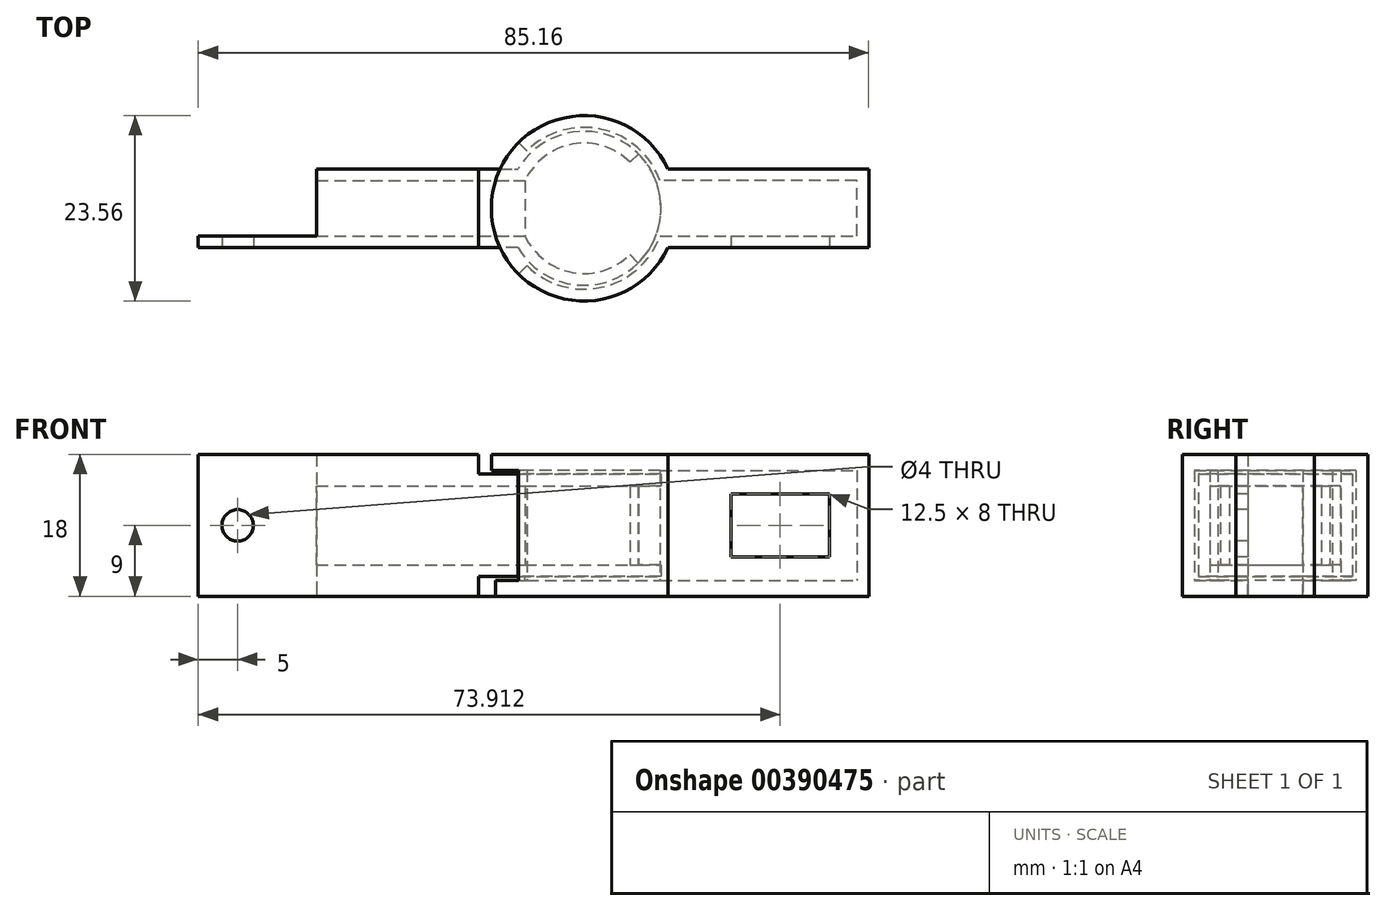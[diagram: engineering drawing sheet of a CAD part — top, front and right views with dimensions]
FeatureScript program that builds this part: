
annotation { "Feature Type Name" : "Feature", "Feature Type Description" : "" }
export const myFeature = defineFeature(function(context is Context, id is Id, definition is map)
    precondition{}
    {
        {
            var Q0;
            Q0=qCreatedBy(makeId("Top.planeOp"),FACE);
            var sketch = newSketch(context, id + "F0", { "sketchPlane" : qUnion([Q0])});
            skLineSegment(sketch, "E0.bottom", {"start": v(-25, 3.5) * mm, "end": v(0, 3.5) * mm});
            skLineSegment(sketch, "E0.top", {"start": v(-25, -3.5) * mm, "end": v(0, -3.5) * mm});
            skLineSegment(sketch, "E0.left", {"start": v(-25, 3.5) * mm, "end": v(-25, -3.5) * mm});
            skLineSegment(sketch, "E0.right", {"start": v(0, 3.5) * mm, "end": v(0, -3.5) * mm});
            skArc(sketch, "E1", {"start": v(0, -3.5) * mm, "mid": v(6.06, -8.15) * mm, "end": v(13.35, -5.85) * mm});
            skPoint(sketch, "E1.centerSnap0", {"position": v(0, 0) * mm});
            skLineSegment(sketch, "E2.left", {"start": v(-25, -3.5) * mm, "end": v(-25, 4) * mm});
            skLineSegment(sketch, "E3", {"start": v(7.5, 0) * mm, "end": v(13.35, 5.85) * mm});
            skLineSegment(sketch, "E4", {"start": v(7.5, 0) * mm, "end": v(13.35, -5.85) * mm});
            skLineSegment(sketch, "E5", {"start": v(7.5, 0) * mm, "end": v(15.78, 0) * mm});
            skArc(sketch, "E6.trimOffspring", {"start": v(13.35, 5.85) * mm, "mid": v(6.06, 8.15) * mm, "end": v(0, 3.5) * mm});
            skArc(sketch, "E7.0", {"start": v(14.41, 6.91) * mm, "mid": v(6.29, 9.7) * mm, "end": v(-0.9, 5) * mm});
            skArc(sketch, "E7.1", {"start": v(-0.9, -5) * mm, "mid": v(6.25, -9.7) * mm, "end": v(14.36, -6.97) * mm});
            skLineSegment(sketch, "E7.2", {"start": v(-26.5, -5) * mm, "end": v(-0.9, -5) * mm});
            skLineSegment(sketch, "E7.3", {"start": v(-26.5, 5) * mm, "end": v(-26.5, -5) * mm});
            skLineSegment(sketch, "E7.4", {"start": v(-26.5, 5) * mm, "end": v(-0.9, 5) * mm});
            skLineSegment(sketch, "E8", {"start": v(13.35, 5.85) * mm, "end": v(14.41, 6.91) * mm});
            skLineSegment(sketch, "E9", {"start": v(13.35, -5.85) * mm, "end": v(14.36, -6.97) * mm});
            skLineSegment(sketch, "E10.bottom", {"start": v(-26.5, -5) * mm, "end": v(-41.5, -5) * mm});
            skLineSegment(sketch, "E10.top", {"start": v(-26.5, -3.5) * mm, "end": v(-41.5, -3.5) * mm});
            skLineSegment(sketch, "E10.left", {"start": v(-26.5, -5) * mm, "end": v(-26.5, -3.5) * mm});
            skLineSegment(sketch, "E10.right", {"start": v(-41.5, -5) * mm, "end": v(-41.5, -3.5) * mm});
            skArc(sketch, "E11", {"start": v(14.41, 6.91) * mm, "mid": v(17.28, -0.04) * mm, "end": v(14.36, -6.97) * mm});
            skLineSegment(sketch, "E12", {"start": v(-5.9, 5) * mm, "end": v(-5.9, -5) * mm});
            skSolve(sketch);
        }
        {
            var Q0;
            Q0=qCreatedBy(makeId("Top.planeOp"),FACE);
            cPlane(context, id + "F1", {"entities" : qUnion([Q0]), "cplaneType" : CPlaneType.OFFSET, "offset" : 0.5 * mm, "oppositeDirection" : true, "width" : 150 * mm, "height" : 150 * mm});
        }
        {
            var Q0;
            Q0=qCreatedBy(id+"F1.planeOp",FACE);
            var sketch = newSketch(context, id + "F2", { "sketchPlane" : qUnion([Q0])});
            skPoint(sketch, "E13.0", {"position": v(7.5, 0) * mm});
            skArc(sketch, "E14.0", {"start": v(14.41, 6.91) * mm, "mid": v(6.29, 9.7) * mm, "end": v(-0.9, 5) * mm});
            skArc(sketch, "E15", {"start": v(17.16, 3.5) * mm, "mid": v(9.73, 10.03) * mm, "end": v(0.23, 7.27) * mm});
            skLineSegment(sketch, "E16", {"start": v(7.5, 0) * mm, "end": v(0.23, 7.27) * mm});
            skLineSegment(sketch, "E17", {"start": v(7.5, 0) * mm, "end": v(0.23, -7.27) * mm});
            skLineSegment(sketch, "E18", {"start": v(7.5, 0) * mm, "end": v(-2.78, 0) * mm});
            skLineSegment(sketch, "E19", {"start": v(17.16, -3.5) * mm, "end": v(42.16, -3.5) * mm});
            skLineSegment(sketch, "E20", {"start": v(42.16, -3.5) * mm, "end": v(42.16, 3.5) * mm});
            skLineSegment(sketch, "E21", {"start": v(42.16, 3.5) * mm, "end": v(17.16, 3.5) * mm});
            skArc(sketch, "E22.trimOffspring", {"start": v(0.23, -7.27) * mm, "mid": v(9.73, -10.03) * mm, "end": v(17.16, -3.5) * mm});
            skArc(sketch, "E23.0", {"start": v(18.16, 5) * mm, "mid": v(9.53, 11.6) * mm, "end": v(-0.83, 8.33) * mm});
            skArc(sketch, "E23.1", {"start": v(-0.83, -8.33) * mm, "mid": v(9.53, -11.6) * mm, "end": v(18.16, -5) * mm});
            skLineSegment(sketch, "E23.2", {"start": v(18.16, -5) * mm, "end": v(43.66, -5) * mm});
            skLineSegment(sketch, "E23.3", {"start": v(43.66, -5) * mm, "end": v(43.66, 5) * mm});
            skLineSegment(sketch, "E23.4", {"start": v(43.66, 5) * mm, "end": v(18.16, 5) * mm});
            skLineSegment(sketch, "E24", {"start": v(0.23, 7.27) * mm, "end": v(-0.83, 8.33) * mm});
            skLineSegment(sketch, "E25", {"start": v(-0.83, -8.33) * mm, "end": v(0.23, -7.27) * mm});
            skPoint(sketch, "E26", {"position": v(42.16, 0) * mm});
            skArc(sketch, "E27", {"start": v(-0.83, 8.33) * mm, "mid": v(-4.28, 0) * mm, "end": v(-0.83, -8.33) * mm});
            skSolve(sketch);
        }
        {
            var Q0;
            Q0=makeQuery(id+"F0.imprint","IMPRINT",FACE,{"disambiguationData":[TD([[makeQuery(id+"F0.imprint","IMPRINT",EDGE,{"derivedFrom":sQuery(id+"F0.wireOp",EDGE,"E0.bottom")}),1.0]])]});
            var Q1;
            Q1=makeQuery(id+"F0.imprint","IMPRINT",FACE,{"disambiguationData":[TD([[makeQuery(id+"F0.imprint","IMPRINT",EDGE,{"derivedFrom":sQuery(id+"F0.wireOp",EDGE,"E10.bottom")}),-1.0]])]});
            var Q2;
            {var subQ0=sQuery(id+"F0.wireOp",EDGE,"E0.left");Q2=makeQuery(id+"F0.imprint","IMPRINT",FACE,{"disambiguationData":[TD([[makeQuery(id+"F0.imprint","IMPRINT",EDGE,{"derivedFrom":subQ0}),-1.0]])]});}
            var Q3;
            {var subQ4=sQuery(id+"F0.wireOp",EDGE,"E1");Q3=makeQuery(id+"F0.imprint","IMPRINT",FACE,{"disambiguationData":[TD([[makeQuery(id+"F0.imprint","IMPRINT",EDGE,{"derivedFrom":subQ4}),-1.0]])]});}
            var Q4;
            {var subQ13=sQuery(id+"F0.wireOp",EDGE,"E7.3");Q4=makeQuery(id+"F0.imprint","IMPRINT",FACE,{"disambiguationData":[TD([[makeQuery(id+"F0.imprint","IMPRINT",EDGE,{"derivedFrom":subQ13}),1.0]])]});}
            extrude(context, id + "F3", {"entities" : qUnion([Q0, Q1, Q2, Q3, Q4]), "depth" : 11.5 * mm});
        }
        {
            var Q0;
            Q0=makeQuery(id+"F3.opExtrude","CAP_FACE",FACE,{"disambiguationData":[OSD([sQuery(id+"F0.wireOp",EDGE,"E10.bottom"),sQuery(id+"F0.wireOp",EDGE,"E10.top"),sQuery(id+"F0.wireOp",EDGE,"E10.left"),sQuery(id+"F0.wireOp",EDGE,"E10.right")])],"isStart":false});
            var Q1;
            {var subQ0=sQuery(id+"F0.wireOp",EDGE,"E0.left");Q1=makeQuery(id+"F0.imprint","IMPRINT",FACE,{"disambiguationData":[TD([[makeQuery(id+"F0.imprint","IMPRINT",EDGE,{"derivedFrom":subQ0}),-1.0]])]});}
            var Q2;
            Q2=makeQuery(id+"F3.opExtrude","CAP_FACE",FACE,{"disambiguationData":[OSD([sQuery(id+"F0.wireOp",EDGE,"E0.bottom"),sQuery(id+"F0.wireOp",EDGE,"E6.trimOffspring"),sQuery(id+"F0.wireOp",EDGE,"E7.0"),sQuery(id+"F0.wireOp",EDGE,"E7.4"),sQuery(id+"F0.wireOp",EDGE,"E8"),sQuery(id+"F0.wireOp",EDGE,"E12")])],"isStart":false});
            var Q3;
            {var subQ4=sQuery(id+"F0.wireOp",EDGE,"E1");Q3=makeQuery(id+"F0.imprint","IMPRINT",FACE,{"disambiguationData":[TD([[makeQuery(id+"F0.imprint","IMPRINT",EDGE,{"derivedFrom":subQ4}),-1.0]])]});}
            var Q4;
            Q4=makeQuery(id+"F0.imprint","IMPRINT",FACE,{"disambiguationData":[TD([[makeQuery(id+"F0.imprint","IMPRINT",EDGE,{"derivedFrom":sQuery(id+"F0.wireOp",EDGE,"E0.right")}),1.0]])]});
            var Q5;
            Q5=makeQuery(id+"F0.imprint","IMPRINT",FACE,{"disambiguationData":[TD([[makeQuery(id+"F0.imprint","IMPRINT",EDGE,{"derivedFrom":sQuery(id+"F0.wireOp",EDGE,"E3")}),-1.0]])]});
            var Q6;
            {var subQ0=sQuery(id+"F0.wireOp",EDGE,"E0.left");Q6=makeQuery(id+"F0.imprint","IMPRINT",FACE,{"disambiguationData":[TD([[makeQuery(id+"F0.imprint","IMPRINT",EDGE,{"derivedFrom":subQ0}),1.0]])]});}
            var Q7;
            {var subQ0=sQuery(id+"F0.wireOp",EDGE,"E0.right");Q7=makeQuery(id+"F0.imprint","IMPRINT",FACE,{"disambiguationData":[TD([[makeQuery(id+"F0.imprint","IMPRINT",EDGE,{"derivedFrom":subQ0}),-1.0]])]});}
            var Q8;
            {var subQ0=sQuery(id+"F0.wireOp",EDGE,"E2.left");var subQ1=sQuery(id+"F0.wireOp",EDGE,"E0.bottom");var subQ2=makeQuery(id+"F0.imprint","INTERSECT",VERTEX,{"derivedFrom":[subQ1,subQ0]});Q8=makeQuery(id+"F0.imprint","IMPRINT",FACE,{"disambiguationData":[TD([[makeQuery(id+"F0.imprint","IMPRINT",EDGE,{"disambiguationData":[TD([[subQ2,-1.0]])],"derivedFrom":subQ1}),-1.0]])]});}
            extrude(context, id + "F4", {"entities" : qUnion([Q0, Q1, Q2, Q3, Q4, Q5, Q6, Q7, Q8]), "operationType" : NewBodyOperationType.ADD, "depth" : 1.5 * mm});
        }
        {
            var Q0;
            Q0=makeQuery(id+"F3.opExtrude","CAP_FACE",FACE,{"disambiguationData":[OSD([sQuery(id+"F0.wireOp",EDGE,"E0.bottom"),sQuery(id+"F0.wireOp",EDGE,"E0.top"),sQuery(id+"F0.wireOp",EDGE,"E0.left"),sQuery(id+"F0.wireOp",EDGE,"E1"),sQuery(id+"F0.wireOp",EDGE,"E2.left"),sQuery(id+"F0.wireOp",EDGE,"E6.trimOffspring"),sQuery(id+"F0.wireOp",EDGE,"E7.0"),sQuery(id+"F0.wireOp",EDGE,"E7.1"),sQuery(id+"F0.wireOp",EDGE,"E7.2"),sQuery(id+"F0.wireOp",EDGE,"E7.3"),sQuery(id+"F0.wireOp",EDGE,"E7.4"),sQuery(id+"F0.wireOp",EDGE,"E8"),sQuery(id+"F0.wireOp",EDGE,"E9"),sQuery(id+"F0.wireOp",EDGE,"E10.bottom"),sQuery(id+"F0.wireOp",EDGE,"E10.top"),sQuery(id+"F0.wireOp",EDGE,"E10.right")])],"isStart":false});
            var Q1;
            Q1=makeQuery(id+"F4.opExtrude","CAP_FACE",FACE,{"disambiguationData":[OSD([sQuery(id+"F0.wireOp",EDGE,"E0.bottom"),sQuery(id+"F0.wireOp",EDGE,"E0.top"),sQuery(id+"F0.wireOp",EDGE,"E0.left"),sQuery(id+"F0.wireOp",EDGE,"E1"),sQuery(id+"F0.wireOp",EDGE,"E2.left"),sQuery(id+"F0.wireOp",EDGE,"E6.trimOffspring"),sQuery(id+"F0.wireOp",EDGE,"E7.0"),sQuery(id+"F0.wireOp",EDGE,"E7.1"),sQuery(id+"F0.wireOp",EDGE,"E7.2"),sQuery(id+"F0.wireOp",EDGE,"E7.3"),sQuery(id+"F0.wireOp",EDGE,"E7.4"),sQuery(id+"F0.wireOp",EDGE,"E8"),sQuery(id+"F0.wireOp",EDGE,"E9"),sQuery(id+"F0.wireOp",EDGE,"E10.bottom"),sQuery(id+"F0.wireOp",EDGE,"E10.top"),sQuery(id+"F0.wireOp",EDGE,"E10.right")])],"isStart":false});
            cPlane(context, id + "F5", {"entities" : qUnion([Q0, Q1]), "cplaneType" : CPlaneType.OFFSET, "offset" : 0 * mm, "width" : 150 * mm, "height" : 150 * mm});
        }
        {
            var Q0;
            Q0=qCreatedBy(id+"F5.planeOp",FACE);
            var sketch = newSketch(context, id + "F6", { "sketchPlane" : qUnion([Q0])});
            skLineSegment(sketch, "E28.0", {"start": v(-26.5, -5) * mm, "end": v(-0.9, -5) * mm});
            skLineSegment(sketch, "E29.0", {"start": v(-26.5, 5) * mm, "end": v(-26.5, -5) * mm});
            skLineSegment(sketch, "E30.0", {"start": v(-26.5, 5) * mm, "end": v(-0.9, 5) * mm});
            skArc(sketch, "E31.0", {"start": v(14.41, 6.91) * mm, "mid": v(6.29, 9.7) * mm, "end": v(-0.9, 5) * mm});
            skArc(sketch, "E32.0", {"start": v(14.41, 6.91) * mm, "mid": v(17.28, -0.04) * mm, "end": v(14.36, -6.97) * mm});
            skArc(sketch, "E33.0", {"start": v(-0.9, -5) * mm, "mid": v(6.25, -9.7) * mm, "end": v(14.36, -6.97) * mm});
            skLineSegment(sketch, "E34.0", {"start": v(-5.9, 5) * mm, "end": v(-5.9, -5) * mm});
            skLineSegment(sketch, "E35.0", {"start": v(-26.5, -3.5) * mm, "end": v(-41.5, -3.5) * mm});
            skPoint(sketch, "E36.0", {"position": v(-41.5, -4.25) * mm});
            skLineSegment(sketch, "E37.0", {"start": v(-26.5, -5) * mm, "end": v(-41.5, -5) * mm});
            skLineSegment(sketch, "E38.0", {"start": v(-41.5, -5) * mm, "end": v(-41.5, -3.5) * mm});
            skSolve(sketch);
        }
        {
            var Q0;
            Q0=makeQuery(id+"F6.imprint","IMPRINT",FACE,{"disambiguationData":[TD([[makeQuery(id+"F6.imprint","IMPRINT",EDGE,{"derivedFrom":sQuery(id+"F6.wireOp",EDGE,"E28.0")}),1.0]])]});
            var Q1;
            {var subQ0=sQuery(id+"F6.wireOp",EDGE,"E31.0");Q1=makeQuery(id+"F6.imprint","IMPRINT",FACE,{"disambiguationData":[TD([[makeQuery(id+"F6.imprint","IMPRINT",EDGE,{"derivedFrom":subQ0}),1.0]])]});}
            extrude(context, id + "F7", {"entities" : qUnion([Q0, Q1]), "operationType" : NewBodyOperationType.ADD, "oppositeDirection" : true, "depth" : 1.5 * mm});
        }
        {
            var Q0;
            {var subQ0=sQuery(id+"F0.wireOp",EDGE,"E7.3");Q0=makeQuery(id+"F4.boolean.opBoolean","MERGE",FACE,{"derivedFrom":[makeQuery(id+"F3.opExtrude","SWEPT_FACE",FACE,{"disambiguationData":[OSD([subQ0])]}),makeQuery(id+"F4.opExtrude","SWEPT_FACE",FACE,{"disambiguationData":[OSD([subQ0])]})]});}
            var sketch = newSketch(context, id + "F8", { "sketchPlane" : qUnion([Q0])});
            skLineSegment(sketch, "E39.bottom", {"start": v(3.5, 1.5) * mm, "end": v(-3.5, 1.5) * mm});
            skLineSegment(sketch, "E40", {"start": v(-3.5, 1.5) * mm, "end": v(-3.5, 11.5) * mm});
            skLineSegment(sketch, "E41", {"start": v(-3.5, 11.5) * mm, "end": v(3.5, 11.5) * mm});
            skLineSegment(sketch, "E42", {"start": v(3.5, 11.5) * mm, "end": v(3.5, 1.5) * mm});
            skLineSegment(sketch, "E43.bottom", {"start": v(-5, 13) * mm, "end": v(3.5, 13) * mm});
            skLineSegment(sketch, "E43.top", {"start": v(-5, 0) * mm, "end": v(3.5, 0) * mm});
            skLineSegment(sketch, "E43.left", {"start": v(-5, 13) * mm, "end": v(-5, 0) * mm});
            skLineSegment(sketch, "E43.right", {"start": v(3.5, 13) * mm, "end": v(3.5, 0) * mm});
            skSolve(sketch);
        }
        {
            var Q0;
            Q0=makeQuery(id+"F8.imprint","IMPRINT",FACE,{"disambiguationData":[TD([[makeQuery(id+"F8.imprint","IMPRINT",EDGE,{"derivedFrom":sQuery(id+"F8.wireOp",EDGE,"E39.bottom")}),-1.0]])]});
            extrude(context, id + "F9", {"entities" : qUnion([Q0]), "operationType" : NewBodyOperationType.REMOVE, "endBound" : BoundingType.UP_TO_NEXT, "oppositeDirection" : true, "depth" : 25 * mm});
        }
        {
            var Q0;
            Q0=makeQuery(id+"F2.imprint","IMPRINT",FACE,{"disambiguationData":[TD([[makeQuery(id+"F2.imprint","IMPRINT",EDGE,{"derivedFrom":sQuery(id+"F2.wireOp",EDGE,"E15")}),-1.0]])]});
            extrude(context, id + "F10", {"entities" : qUnion([Q0]), "depth" : 14 * mm});
        }
        {
            var Q0;
            Q0=makeQuery(id+"F2.imprint","IMPRINT",FACE,{"disambiguationData":[TD([[makeQuery(id+"F2.imprint","IMPRINT",EDGE,{"derivedFrom":sQuery(id+"F2.wireOp",EDGE,"E15")}),-1.0]])]});
            var Q1;
            {var subQ2=sQuery(id+"F2.wireOp",EDGE,"E15");Q1=makeQuery(id+"F2.imprint","IMPRINT",FACE,{"disambiguationData":[TD([[makeQuery(id+"F2.imprint","IMPRINT",EDGE,{"derivedFrom":subQ2}),1.0]])]});}
            var Q2;
            {var subQ3=sQuery(id+"F2.wireOp",EDGE,"E17");Q2=makeQuery(id+"F2.imprint","IMPRINT",FACE,{"disambiguationData":[TD([[makeQuery(id+"F2.imprint","IMPRINT",EDGE,{"derivedFrom":subQ3}),-1.0]])]});}
            extrude(context, id + "F11", {"entities" : qUnion([Q0, Q1, Q2]), "operationType" : NewBodyOperationType.ADD, "oppositeDirection" : true, "depth" : 2 * mm});
        }
        {
            var Q0;
            Q0=makeQuery(id+"F10.opExtrude","CAP_FACE",FACE,{"disambiguationData":[OSD([sQuery(id+"F2.wireOp",EDGE,"E15"),sQuery(id+"F2.wireOp",EDGE,"E19"),sQuery(id+"F2.wireOp",EDGE,"E20"),sQuery(id+"F2.wireOp",EDGE,"E21"),sQuery(id+"F2.wireOp",EDGE,"E22.trimOffspring"),sQuery(id+"F2.wireOp",EDGE,"E23.0"),sQuery(id+"F2.wireOp",EDGE,"E23.1"),sQuery(id+"F2.wireOp",EDGE,"E23.2"),sQuery(id+"F2.wireOp",EDGE,"E23.3"),sQuery(id+"F2.wireOp",EDGE,"E23.4"),sQuery(id+"F2.wireOp",EDGE,"E24"),sQuery(id+"F2.wireOp",EDGE,"E25")])],"isStart":false});
            cPlane(context, id + "F12", {"entities" : qUnion([Q0]), "cplaneType" : CPlaneType.OFFSET, "offset" : 0 * mm, "width" : 150 * mm, "height" : 150 * mm});
        }
        {
            var Q0;
            Q0=qCreatedBy(id+"F12.planeOp",FACE);
            var sketch = newSketch(context, id + "F13", { "sketchPlane" : qUnion([Q0])});
            skLineSegment(sketch, "E44.0", {"start": v(43.66, 5) * mm, "end": v(18.16, 5) * mm});
            skLineSegment(sketch, "E45.0", {"start": v(43.66, -5) * mm, "end": v(43.66, 5) * mm});
            skLineSegment(sketch, "E46.0", {"start": v(18.16, -5) * mm, "end": v(43.66, -5) * mm});
            skArc(sketch, "E47.0", {"start": v(-0.83, -8.33) * mm, "mid": v(9.53, -11.6) * mm, "end": v(18.16, -5) * mm});
            skArc(sketch, "E48.0", {"start": v(-0.83, 8.33) * mm, "mid": v(-4.28, 0) * mm, "end": v(-0.83, -8.33) * mm});
            skArc(sketch, "E49.0", {"start": v(18.16, 5) * mm, "mid": v(9.53, 11.6) * mm, "end": v(-0.83, 8.33) * mm});
            skLineSegment(sketch, "E50.0", {"start": v(-5.9, 5) * mm, "end": v(-5.9, -5) * mm});
            skSolve(sketch);
        }
        {
            var Q0;
            Q0=makeQuery(id+"F13.imprint","IMPRINT",FACE,{"disambiguationData":[TD([[makeQuery(id+"F13.imprint","IMPRINT",EDGE,{"derivedFrom":sQuery(id+"F13.wireOp",EDGE,"E44.0")}),1.0]])]});
            extrude(context, id + "F14", {"entities" : qUnion([Q0]), "operationType" : NewBodyOperationType.ADD, "depth" : 2 * mm});
        }
        {
            var Q0;
            Q0=makeQuery(id+"F3.opExtrude","SWEPT_FACE",FACE,{"disambiguationData":[OSD([sQuery(id+"F0.wireOp",EDGE,"E7.2"),sQuery(id+"F0.wireOp",EDGE,"E10.bottom")])]});
            var sketch = newSketch(context, id + "F15", { "sketchPlane" : qUnion([Q0])});
            skPoint(sketch, "E51", {"position": v(-41.5, 6.5) * mm});
            skPoint(sketch, "E52", {"position": v(-36.5, 6.5) * mm});
            skCircle(sketch, "E53", {"center": v(-36.5, 6.5) * mm, "radius": 2 * mm});
            skSolve(sketch);
        }
        {
            var Q0;
            Q0=makeQuery(id+"F15.imprint","IMPRINT",FACE,{"disambiguationData":[TD([[makeQuery(id+"F15.imprint","IMPRINT",EDGE,{"derivedFrom":sQuery(id+"F15.wireOp",EDGE,"E53")}),1.0]])]});
            extrude(context, id + "F16", {"entities" : qUnion([Q0]), "operationType" : NewBodyOperationType.REMOVE, "endBound" : BoundingType.UP_TO_NEXT, "oppositeDirection" : true, "depth" : 25 * mm});
        }
        {
            var Q0;
            {var subQ0=sQuery(id+"F2.wireOp",EDGE,"E23.2");Q0=makeQuery(id+"F14.boolean.opBoolean","MERGE",FACE,{"derivedFrom":[makeQuery(id+"F11.boolean.opBoolean","MERGE",FACE,{"derivedFrom":[makeQuery(id+"F10.opExtrude","SWEPT_FACE",FACE,{"disambiguationData":[OSD([subQ0])]}),makeQuery(id+"F11.opExtrude","SWEPT_FACE",FACE,{"disambiguationData":[OSD([subQ0])]})]}),makeQuery(id+"F14.opExtrude","SWEPT_FACE",FACE,{"disambiguationData":[OSD([sQuery(id+"F13.wireOp",EDGE,"E46.0")])]})]});}
            var sketch = newSketch(context, id + "F17", { "sketchPlane" : qUnion([Q0])});
            skLineSegment(sketch, "E54.bottom", {"start": v(18.16, 15.5) * mm, "end": v(43.66, 15.5) * mm});
            skLineSegment(sketch, "E54.top", {"start": v(18.16, -2.5) * mm, "end": v(43.66, -2.5) * mm});
            skLineSegment(sketch, "E54.left", {"start": v(18.16, 15.5) * mm, "end": v(18.16, -2.5) * mm});
            skLineSegment(sketch, "E54.right", {"start": v(43.66, 15.5) * mm, "end": v(43.66, -2.5) * mm});
            skLineSegment(sketch, "E55.bottom", {"start": v(26.16, 10.5) * mm, "end": v(38.66, 10.5) * mm});
            skLineSegment(sketch, "E55.top", {"start": v(26.16, 2.5) * mm, "end": v(38.66, 2.5) * mm});
            skLineSegment(sketch, "E55.left", {"start": v(26.16, 10.5) * mm, "end": v(26.16, 2.5) * mm});
            skLineSegment(sketch, "E55.right", {"start": v(38.66, 10.5) * mm, "end": v(38.66, 2.5) * mm});
            skSolve(sketch);
        }
        {
            var Q0;
            Q0=makeQuery(id+"F17.imprint","IMPRINT",FACE,{"disambiguationData":[TD([[makeQuery(id+"F17.imprint","IMPRINT",EDGE,{"derivedFrom":sQuery(id+"F17.wireOp",EDGE,"E55.bottom")}),-1.0]])]});
            extrude(context, id + "F18", {"entities" : qUnion([Q0]), "operationType" : NewBodyOperationType.REMOVE, "endBound" : BoundingType.UP_TO_NEXT, "oppositeDirection" : true, "depth" : 25 * mm});
        }
        {
            var Q0;
            {var subQ0=sQuery(id+"F0.wireOp",EDGE,"E0.left");Q0=makeQuery(id+"F0.imprint","IMPRINT",FACE,{"disambiguationData":[TD([[makeQuery(id+"F0.imprint","IMPRINT",EDGE,{"derivedFrom":subQ0}),-1.0]])]});}
            var Q1;
            {var subQ0=sQuery(id+"F0.wireOp",EDGE,"E0.left");Q1=makeQuery(id+"F0.imprint","IMPRINT",FACE,{"disambiguationData":[TD([[makeQuery(id+"F0.imprint","IMPRINT",EDGE,{"derivedFrom":subQ0}),1.0]])]});}
            var Q2;
            Q2=makeQuery(id+"F0.imprint","IMPRINT",FACE,{"disambiguationData":[TD([[makeQuery(id+"F0.imprint","IMPRINT",EDGE,{"derivedFrom":sQuery(id+"F0.wireOp",EDGE,"E10.bottom")}),-1.0]])]});
            var Q3;
            {var subQ13=sQuery(id+"F0.wireOp",EDGE,"E7.3");Q3=makeQuery(id+"F0.imprint","IMPRINT",FACE,{"disambiguationData":[TD([[makeQuery(id+"F0.imprint","IMPRINT",EDGE,{"derivedFrom":subQ13}),1.0]])]});}
            var Q4;
            {var subQ0=sQuery(id+"F0.wireOp",EDGE,"E2.left");var subQ1=sQuery(id+"F0.wireOp",EDGE,"E0.bottom");var subQ2=makeQuery(id+"F0.imprint","INTERSECT",VERTEX,{"derivedFrom":[subQ1,subQ0]});Q4=makeQuery(id+"F0.imprint","IMPRINT",FACE,{"disambiguationData":[TD([[makeQuery(id+"F0.imprint","IMPRINT",EDGE,{"disambiguationData":[TD([[subQ2,-1.0]])],"derivedFrom":subQ1}),-1.0]])]});}
            extrude(context, id + "F19", {"entities" : qUnion([Q0, Q1, Q2, Q3, Q4]), "operationType" : NewBodyOperationType.ADD, "oppositeDirection" : true, "depth" : 2.5 * mm});
        }
        {
            var Q0;
            {var subQ0=sQuery(id+"F6.wireOp",EDGE,"E29.0");Q0=makeQuery(id+"F6.imprint","IMPRINT",FACE,{"disambiguationData":[TD([[makeQuery(id+"F6.imprint","IMPRINT",EDGE,{"derivedFrom":subQ0}),1.0]])]});}
            var Q1;
            {var subQ2=sQuery(id+"F6.wireOp",EDGE,"E35.0");Q1=makeQuery(id+"F6.imprint","IMPRINT",FACE,{"disambiguationData":[TD([[makeQuery(id+"F6.imprint","IMPRINT",EDGE,{"derivedFrom":subQ2}),1.0]])]});}
            extrude(context, id + "F20", {"entities" : qUnion([Q0, Q1]), "operationType" : NewBodyOperationType.ADD, "depth" : 2.5 * mm});
        }
    });
